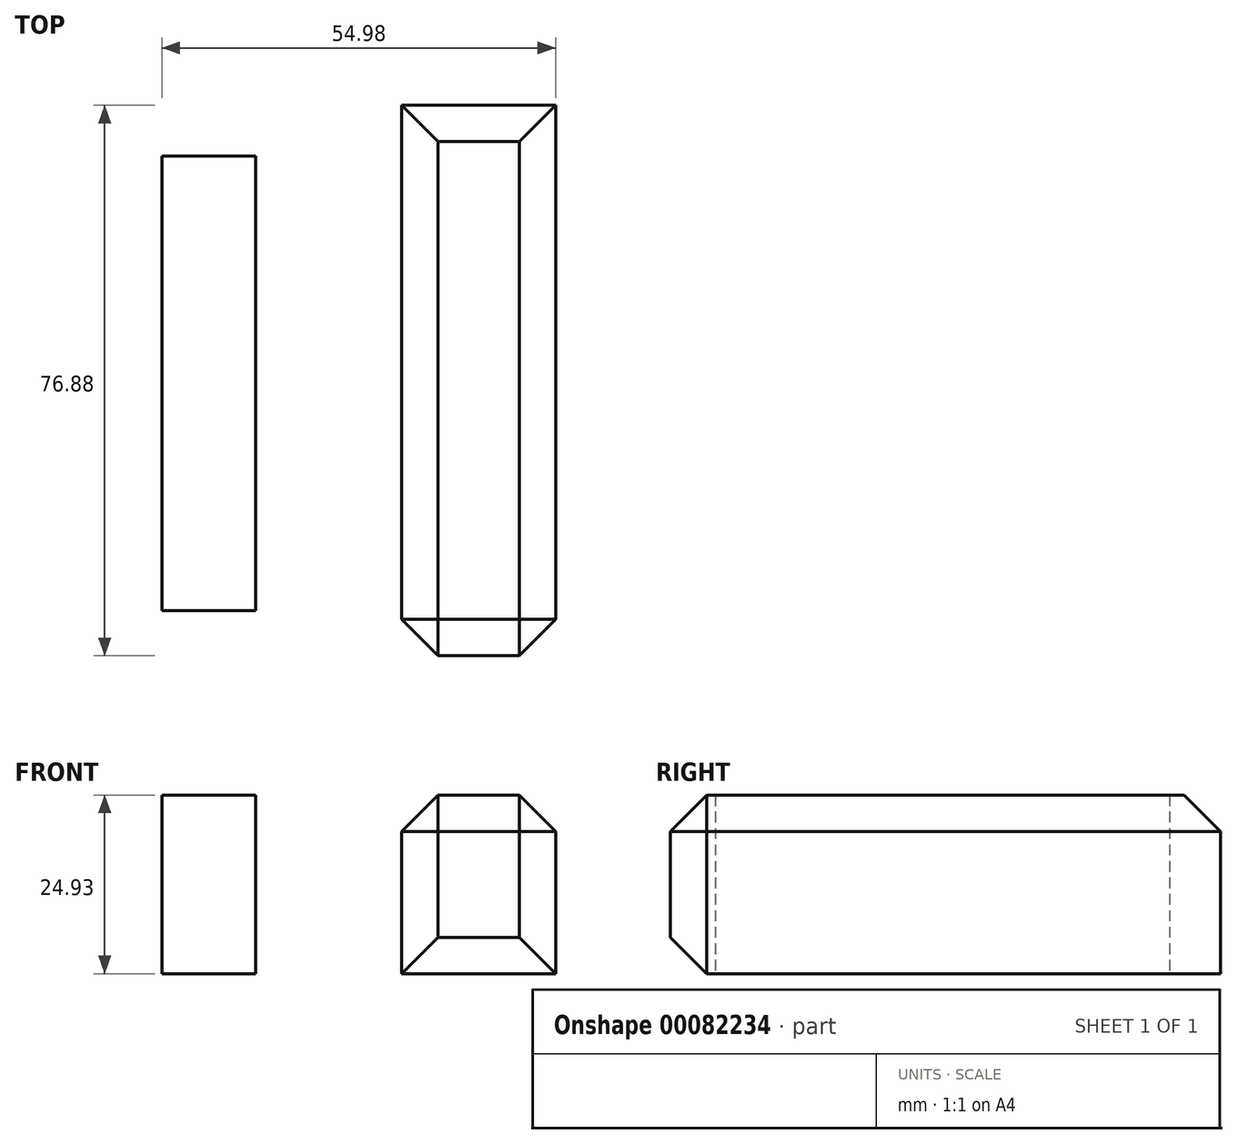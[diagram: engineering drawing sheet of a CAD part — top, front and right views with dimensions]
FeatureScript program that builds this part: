
annotation { "Feature Type Name" : "Feature", "Feature Type Description" : "" }
export const myFeature = defineFeature(function(context is Context, id is Id, definition is map)
    precondition{}
    {
        {
            var Q0;
            Q0=qCreatedBy(makeId("Top.planeOp"),FACE);
            var sketch = newSketch(context, id + "F0", { "sketchPlane" : qUnion([Q0])});
            skLineSegment(sketch, "E0.bottom", {"start": v(-5.79, -38.86) * mm, "end": v(7.32, -38.86) * mm});
            skLineSegment(sketch, "E0.top", {"start": v(-5.79, 24.63) * mm, "end": v(7.32, 24.63) * mm});
            skLineSegment(sketch, "E0.left", {"start": v(-5.79, -38.86) * mm, "end": v(-5.79, 24.63) * mm});
            skLineSegment(sketch, "E0.right", {"start": v(7.32, -38.86) * mm, "end": v(7.32, 24.63) * mm});
            skLineSegment(sketch, "E1.bottom", {"start": v(49.2, 31.75) * mm, "end": v(27.7, 31.75) * mm});
            skLineSegment(sketch, "E1.top", {"start": v(49.2, -45.13) * mm, "end": v(27.7, -45.13) * mm});
            skLineSegment(sketch, "E1.left", {"start": v(49.2, 31.75) * mm, "end": v(49.2, -45.13) * mm});
            skLineSegment(sketch, "E1.right", {"start": v(27.7, 31.75) * mm, "end": v(27.7, -45.13) * mm});
            skSolve(sketch);
        }
        {
            var Q0;
            Q0 = qSketchRegion(id + "F0", true);
            extrude(context, id + "F1", {"entities" : qUnion([Q0]), "depth" : 24.93 * mm});
        }
        {
            var Q0;
            Q0=makeQuery(id+"F1.opExtrude","CAP_FACE",FACE,{"disambiguationData":[OSD([sQuery(id+"F0.wireOp",EDGE,"E1.bottom"),sQuery(id+"F0.wireOp",EDGE,"E1.top"),sQuery(id+"F0.wireOp",EDGE,"E1.left"),sQuery(id+"F0.wireOp",EDGE,"E1.right")])],"isStart":false});
            var Q1;
            Q1=makeQuery(id+"F1.opExtrude","SWEPT_FACE",FACE,{"disambiguationData":[OSD([sQuery(id+"F0.wireOp",EDGE,"E1.top")])]});
            chamfer(context, id + "F2", {"entities" : qUnion([Q0, Q1]), "width" : 5.08 * mm, "tangentPropagation" : true});
        }
    });
